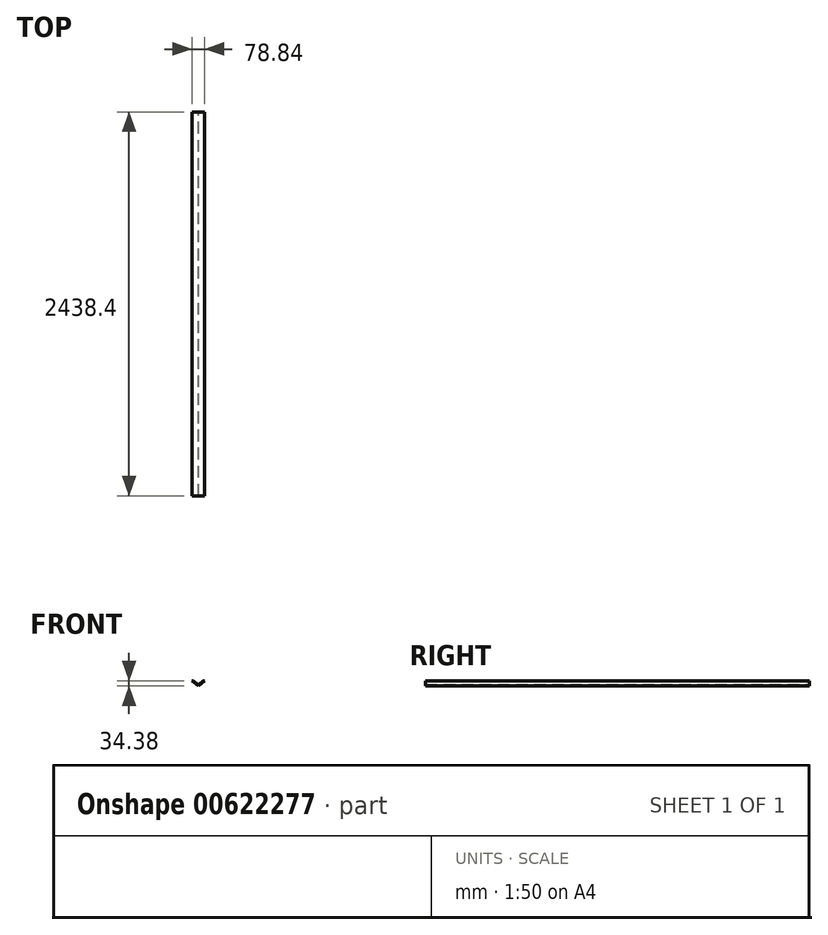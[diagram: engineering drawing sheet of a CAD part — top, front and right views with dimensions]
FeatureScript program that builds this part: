
annotation { "Feature Type Name" : "Feature", "Feature Type Description" : "" }
export const myFeature = defineFeature(function(context is Context, id is Id, definition is map)
    precondition{}
    {
        {
            var Q0;
            Q0=qCreatedBy(makeId("Front.planeOp"),FACE);
            var sketch = newSketch(context, id + "F0", { "sketchPlane" : qUnion([Q0])});
            skLineSegment(sketch, "E0", {"start": v(0, 0) * mm, "end": v(-39.42, 32.04) * mm});
            skLineSegment(sketch, "E1", {"start": v(-39.42, 32.04) * mm, "end": v(-39.42, 32.04) * mm});
            skLineSegment(sketch, "E2", {"start": v(-30.5, 32.96) * mm, "end": v(-5, 12.25) * mm});
            skLineSegment(sketch, "E3", {"start": v(5, 12.25) * mm, "end": v(30.5, 32.96) * mm});
            skLineSegment(sketch, "E4", {"start": v(39.42, 32.04) * mm, "end": v(39.42, 32.04) * mm});
            skLineSegment(sketch, "E5", {"start": v(39.42, 32.04) * mm, "end": v(0, 0) * mm});
            skPoint(sketch, "E6.visualSharp", {"position": v(-35.42, 36.97) * mm});
            skArc(sketch, "E6.filletArc", {"start": v(-30.5, 32.96) * mm, "mid": v(-35.15, 34.35) * mm, "end": v(-39.42, 32.04) * mm});
            skPoint(sketch, "E7.visualSharp", {"position": v(35.42, 36.97) * mm});
            skArc(sketch, "E7.filletArc", {"start": v(39.42, 32.04) * mm, "mid": v(35.15, 34.35) * mm, "end": v(30.5, 32.96) * mm});
            skPoint(sketch, "E8.visualSharp", {"position": v(0, 8.18) * mm});
            skArc(sketch, "E8.filletArc", {"start": v(-5, 12.25) * mm, "mid": v(0, 10.47) * mm, "end": v(5, 12.25) * mm});
            skSolve(sketch);
        }
        {
            var Q0;
            Q0 = qSketchRegion(id + "F0", true);
            extrude(context, id + "F1", {"entities" : qUnion([Q0]), "depth" : 2438.4 * mm, "offsetDistance" : 25.4 * mm});
        }
    });
